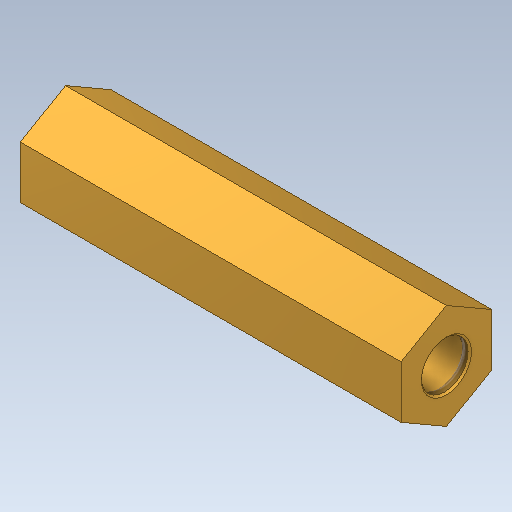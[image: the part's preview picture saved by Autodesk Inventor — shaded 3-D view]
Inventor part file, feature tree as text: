
AUTODESK INVENTOR PART (.ipt)
format: ipt  version: 2021 (Build 250183000, 183)  size: 118,272 bytes
history: native  units: mm
features: other x5, thread x2, revolve x1, chamfer x1
ambient origin geometry x6: Origin, XZ Plane, XY Plane, X Axis, Y Axis, Z Axis
bodies: Solid1 (feature_tree)
feature tree (9):
  revolve  "Revolution1"  [1 undecoded]
  other  "N-Side1"
  thread  "Thread2"  [1 undecoded]
  other  "Start Plane"
  other  "Origin point"
  other  "Main Sketch"
  other  "iFeature1:1"
  thread  "Thread1"  [1 undecoded]
  chamfer  "Chamfer1"  Distance=2.459mm
note: 3 required parameter values undecoded (feature->parameter linkage not recoverable at this tier; creation-order binding heuristic only, values carry confidence <= 0.55)